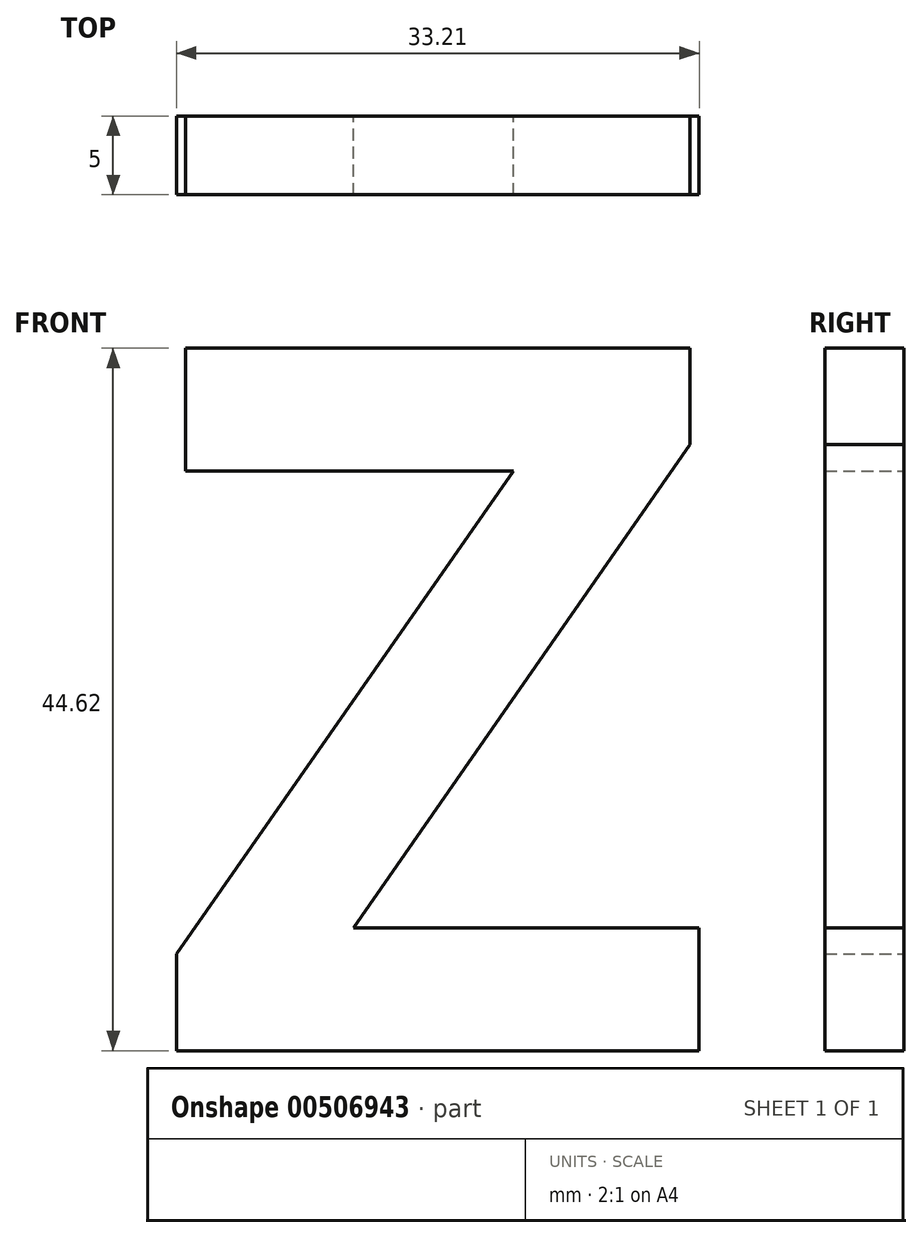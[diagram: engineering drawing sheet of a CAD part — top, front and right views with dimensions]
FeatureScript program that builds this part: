
annotation { "Feature Type Name" : "Feature", "Feature Type Description" : "" }
export const myFeature = defineFeature(function(context is Context, id is Id, definition is map)
    precondition{}
    {
        {
            var Q0;
            Q0=qCreatedBy(makeId("Front.planeOp"),FACE);
            var sketch = newSketch(context, id + "F0", { "sketchPlane" : qUnion([Q0])});
            skText(sketch, "E0", { "text": "Z", "fontName": "OpenSans-Bold.ttf"});
            const initialGuessF0  = {"E0": [-0.06406, 0.00385, 1, 0, 0.045]};
            skSetInitialGuess(sketch, initialGuessF0);
            skSolve(sketch);
        }
        {
            var Q0;
            Q0=makeQuery(id+"F0.imprint","IMPRINT",FACE,{"disambiguationData":[TD([[makeQuery(id+"F0.imprint","IMPRINT",EDGE,{"derivedFrom":sQuery(id+"F0.wireOp",EDGE,"E0.sketch_text.stroke-0")}),-1.0]])]});
            extrude(context, id + "F1", {"entities" : qUnion([Q0]), "depth" : 5 * mm, "offsetDistance" : 25 * mm});
        }
    });
